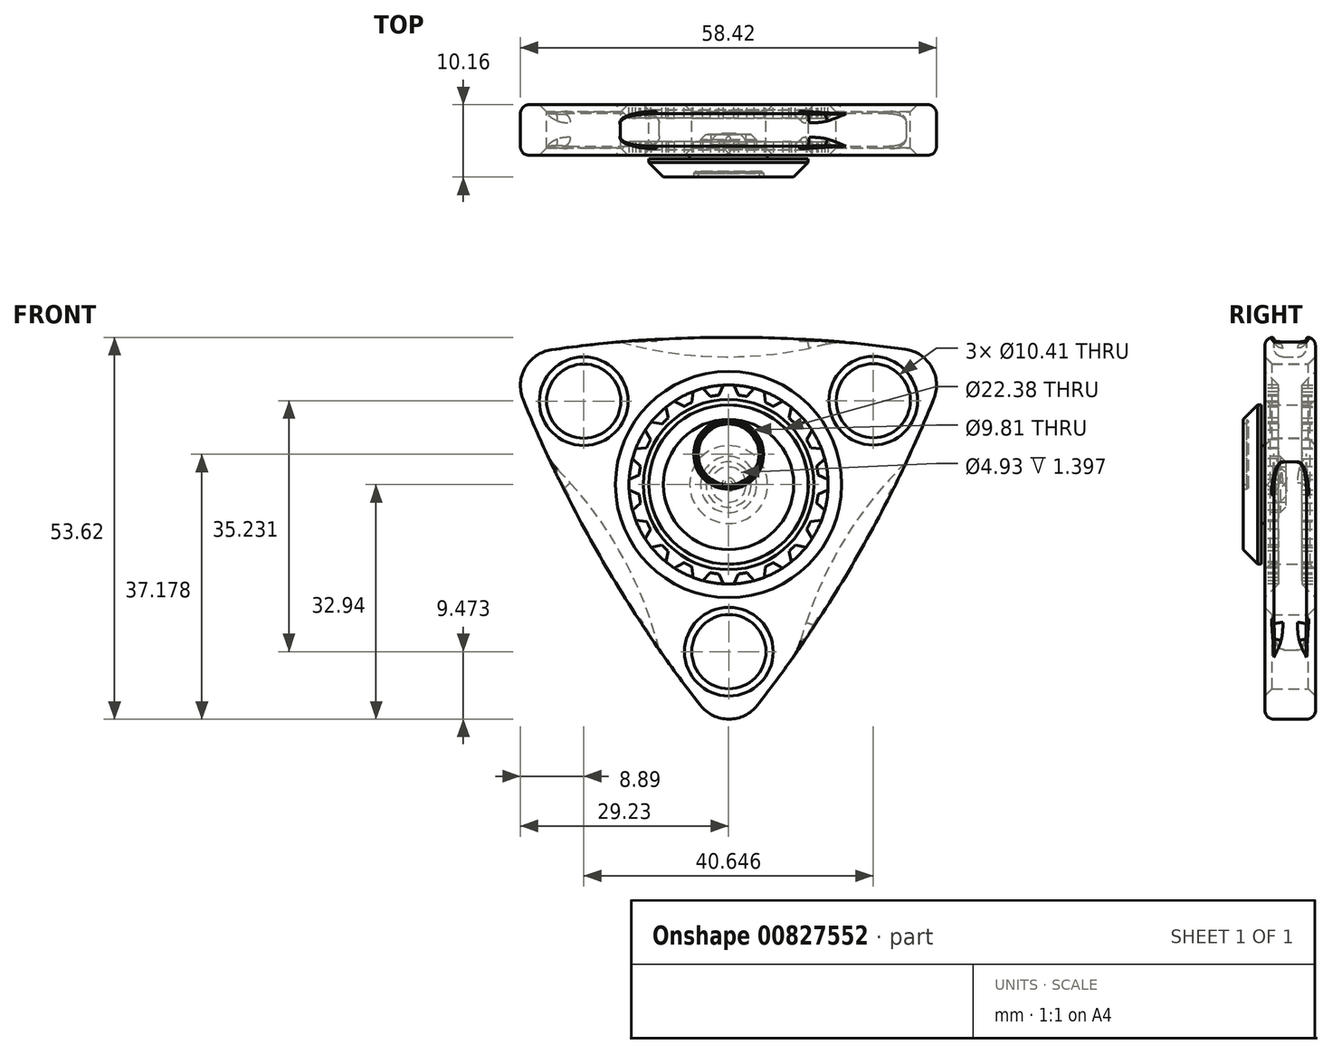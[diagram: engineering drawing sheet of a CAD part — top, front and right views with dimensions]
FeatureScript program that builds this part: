
annotation { "Feature Type Name" : "Feature", "Feature Type Description" : "" }
export const myFeature = defineFeature(function(context is Context, id is Id, definition is map)
    precondition{}
    {
        {
            var Q0;
            Q0=qCreatedBy(makeId("Front.planeOp"),FACE);
            var sketch = newSketch(context, id + "F0", { "sketchPlane" : qUnion([Q0])});
            skCircle(sketch, "E0", {"center": v(0, 0) * mm, "radius": 11.19 * mm});
            skCircle(sketch, "E1", {"center": v(0, 0) * mm, "radius": 14.4 * mm});
            skCircle(sketch, "E2.cCircle", {"center": v(0, 0) * mm, "radius": 17.96 * mm, "construction": true});
            skLineSegment(sketch, "E2.0", {"start": v(-31.13, 17.91) * mm, "end": v(31.08, 18) * mm});
            skLineSegment(sketch, "E2.1", {"start": v(31.08, 18) * mm, "end": v(0.05, -35.92) * mm});
            skLineSegment(sketch, "E2.2", {"start": v(0.05, -35.92) * mm, "end": v(-31.13, 17.91) * mm});
            skPoint(sketch, "E2.0.midPoint", {"position": v(-0.03, 17.96) * mm});
            skArc(sketch, "E3", {"start": v(31.08, 18) * mm, "mid": v(-0.03, 20.7) * mm, "end": v(-31.13, 17.91) * mm});
            skArc(sketch, "E4.1.0", {"start": v(-31.13, 17.91) * mm, "mid": v(-17.92, -10.38) * mm, "end": v(0.05, -35.92) * mm});
            skArc(sketch, "E4.2.0", {"start": v(0.05, -35.92) * mm, "mid": v(17.95, -10.33) * mm, "end": v(31.08, 18) * mm});
            skLineSegment(sketch, "E5", {"start": v(0, 0) * mm, "end": v(-31.13, 17.91) * mm});
            skCircle(sketch, "E6", {"center": v(-20.34, 11.7) * mm, "radius": 5.2 * mm});
            skCircle(sketch, "E7.1.0", {"center": v(0.03, -23.47) * mm, "radius": 5.2 * mm});
            skCircle(sketch, "E7.2.0", {"center": v(20.3, 11.76) * mm, "radius": 5.2 * mm});
            skSolve(sketch);
        }
        {
            var Q0;
            Q0=makeQuery(id+"F0.imprint","IMPRINT",FACE,{"disambiguationData":[TD([[makeQuery(id+"F0.imprint","IMPRINT",EDGE,{"derivedFrom":sQuery(id+"F0.wireOp",EDGE,"E1")}),-1.0]])]});
            var Q1;
            Q1=makeQuery(id+"F0.imprint","IMPRINT",FACE,{"disambiguationData":[TD([[makeQuery(id+"F0.imprint","IMPRINT",EDGE,{"derivedFrom":sQuery(id+"F0.wireOp",EDGE,"E0")}),-1.0]])]});
            var Q2;
            Q2=makeQuery(id+"F0.imprint","IMPRINT",FACE,{"disambiguationData":[TD([[makeQuery(id+"F0.imprint","IMPRINT",EDGE,{"derivedFrom":sQuery(id+"F0.wireOp",EDGE,"E2.2")}),1.0]])]});
            var Q3;
            Q3=makeQuery(id+"F0.imprint","IMPRINT",FACE,{"disambiguationData":[TD([[makeQuery(id+"F0.imprint","IMPRINT",EDGE,{"derivedFrom":sQuery(id+"F0.wireOp",EDGE,"E2.0")}),1.0]])]});
            var Q4;
            Q4=makeQuery(id+"F0.imprint","IMPRINT",FACE,{"disambiguationData":[TD([[makeQuery(id+"F0.imprint","IMPRINT",EDGE,{"derivedFrom":sQuery(id+"F0.wireOp",EDGE,"E2.1")}),1.0]])]});
            extrude(context, id + "F1", {"entities" : qUnion([Q0, Q1, Q2, Q3, Q4]), "depth" : 3.56 * mm, "offsetDistance" : 25.4 * mm});
        }
        {
            var Q0;
            Q0=makeQuery(id+"F1.opExtrude","SWEPT_EDGE",EDGE,{"disambiguationData":[OSD([sQuery(id+"F0.wireOp",EDGE,"E2.0"),sQuery(id+"F0.wireOp",EDGE,"E2.2"),sQuery(id+"F0.wireOp",EDGE,"E3"),sQuery(id+"F0.wireOp",EDGE,"E4.1.0")])]});
            var Q1;
            Q1=makeQuery(id+"F1.opExtrude","SWEPT_EDGE",EDGE,{"disambiguationData":[OSD([sQuery(id+"F0.wireOp",EDGE,"E2.1"),sQuery(id+"F0.wireOp",EDGE,"E2.2"),sQuery(id+"F0.wireOp",EDGE,"E4.1.0"),sQuery(id+"F0.wireOp",EDGE,"E4.2.0")])]});
            var Q2;
            Q2=makeQuery(id+"F1.opExtrude","SWEPT_EDGE",EDGE,{"disambiguationData":[OSD([sQuery(id+"F0.wireOp",EDGE,"E2.0"),sQuery(id+"F0.wireOp",EDGE,"E2.1"),sQuery(id+"F0.wireOp",EDGE,"E3"),sQuery(id+"F0.wireOp",EDGE,"E4.2.0")])]});
            fillet(context, id + "F2", {"entities" : qUnion([Q0, Q1, Q2]), "radius" : 5.08 * mm, "tangentPropagation" : true, "allowEdgeOverflow" : false});
        }
        {
            var Q0;
            Q0=makeQuery(id+"F1.opExtrude","CAP_EDGE",EDGE,{"disambiguationData":[OSD([sQuery(id+"F0.wireOp",EDGE,"E6")])],"isStart":false});
            var Q1;
            Q1=makeQuery(id+"F1.opExtrude","CAP_EDGE",EDGE,{"disambiguationData":[OSD([sQuery(id+"F0.wireOp",EDGE,"E7.2.0")])],"isStart":false});
            var Q2;
            Q2=makeQuery(id+"F1.opExtrude","CAP_EDGE",EDGE,{"disambiguationData":[OSD([sQuery(id+"F0.wireOp",EDGE,"E7.1.0")])],"isStart":false});
            chamfer(context, id + "F3", {"entities" : qUnion([Q0, Q1, Q2]), "width" : 1.02 * mm, "tangentPropagation" : true});
        }
        {
            var Q0;
            Q0=makeQuery(id+"F1.opExtrude","CAP_EDGE",EDGE,{"disambiguationData":[OSD([sQuery(id+"F0.wireOp",EDGE,"E4.2.0")])],"isStart":false});
            var Q1;
            Q1=makeQuery(id+"F1.opExtrude","CAP_EDGE",EDGE,{"disambiguationData":[OSD([sQuery(id+"F0.wireOp",EDGE,"E4.1.0")])],"isStart":false});
            var Q2;
            Q2=makeQuery(id+"F1.opExtrude","CAP_EDGE",EDGE,{"disambiguationData":[OSD([sQuery(id+"F0.wireOp",EDGE,"E3")])],"isStart":false});
            fillet(context, id + "F4", {"entities" : qUnion([Q0, Q1, Q2]), "radius" : 1.27 * mm, "tangentPropagation" : true, "allowEdgeOverflow" : false});
        }
        {
            var Q0;
            Q0=makeQuery(id+"F1.opExtrude","CAP_FACE",FACE,{"disambiguationData":[OSD([sQuery(id+"F0.wireOp",EDGE,"E0"),sQuery(id+"F0.wireOp",EDGE,"E3"),sQuery(id+"F0.wireOp",EDGE,"E4.1.0"),sQuery(id+"F0.wireOp",EDGE,"E4.2.0"),sQuery(id+"F0.wireOp",EDGE,"E6"),sQuery(id+"F0.wireOp",EDGE,"E7.1.0"),sQuery(id+"F0.wireOp",EDGE,"E7.2.0")])],"isStart":false});
            var sketch = newSketch(context, id + "F5", { "sketchPlane" : qUnion([Q0])});
            skCircle(sketch, "E8", {"center": v(0, 0) * mm, "radius": 12.63 * mm});
            skCircle(sketch, "E9", {"center": v(0, 0) * mm, "radius": 15.88 * mm});
            skLineSegment(sketch, "E10", {"start": v(-1.37, 12.56) * mm, "end": v(-0.73, 13.97) * mm});
            skLineSegment(sketch, "E11.MirrorCS", {"start": v(1.37, 12.56) * mm, "end": v(0.73, 13.97) * mm});
            skLineSegment(sketch, "E12", {"start": v(-0.73, 13.97) * mm, "end": v(0.73, 13.97) * mm});
            skLineSegment(sketch, "E13.1.0", {"start": v(-5.19, 11.52) * mm, "end": v(-5, 13.06) * mm});
            skLineSegment(sketch, "E13.1.1", {"start": v(-2.57, 12.37) * mm, "end": v(-3.62, 13.5) * mm});
            skLineSegment(sketch, "E13.1.2", {"start": v(-5, 13.06) * mm, "end": v(-3.62, 13.5) * mm});
            skLineSegment(sketch, "E13.2.0", {"start": v(-8.5, 9.35) * mm, "end": v(-8.8, 10.87) * mm});
            skLineSegment(sketch, "E13.2.1", {"start": v(-6.27, 10.96) * mm, "end": v(-7.62, 11.73) * mm});
            skLineSegment(sketch, "E13.2.2", {"start": v(-8.8, 10.87) * mm, "end": v(-7.62, 11.73) * mm});
            skLineSegment(sketch, "E13.3.0", {"start": v(-10.96, 6.27) * mm, "end": v(-11.73, 7.62) * mm});
            skLineSegment(sketch, "E13.3.1", {"start": v(-9.35, 8.5) * mm, "end": v(-10.87, 8.8) * mm});
            skLineSegment(sketch, "E13.3.2", {"start": v(-11.73, 7.62) * mm, "end": v(-10.87, 8.8) * mm});
            skLineSegment(sketch, "E13.4.0", {"start": v(-12.37, 2.57) * mm, "end": v(-13.5, 3.62) * mm});
            skLineSegment(sketch, "E13.4.1", {"start": v(-11.52, 5.19) * mm, "end": v(-13.06, 5) * mm});
            skLineSegment(sketch, "E13.4.2", {"start": v(-13.5, 3.62) * mm, "end": v(-13.06, 5) * mm});
            skLineSegment(sketch, "E13.5.0", {"start": v(-12.56, -1.37) * mm, "end": v(-13.97, -0.73) * mm});
            skLineSegment(sketch, "E13.5.1", {"start": v(-12.56, 1.37) * mm, "end": v(-13.97, 0.73) * mm});
            skLineSegment(sketch, "E13.5.2", {"start": v(-13.97, -0.73) * mm, "end": v(-13.97, 0.73) * mm});
            skLineSegment(sketch, "E13.6.0", {"start": v(-11.52, -5.19) * mm, "end": v(-13.06, -5) * mm});
            skLineSegment(sketch, "E13.6.1", {"start": v(-12.37, -2.57) * mm, "end": v(-13.5, -3.62) * mm});
            skLineSegment(sketch, "E13.6.2", {"start": v(-13.06, -5) * mm, "end": v(-13.5, -3.62) * mm});
            skLineSegment(sketch, "E13.7.0", {"start": v(-9.35, -8.5) * mm, "end": v(-10.87, -8.8) * mm});
            skLineSegment(sketch, "E13.7.1", {"start": v(-10.96, -6.27) * mm, "end": v(-11.73, -7.62) * mm});
            skLineSegment(sketch, "E13.7.2", {"start": v(-10.87, -8.8) * mm, "end": v(-11.73, -7.62) * mm});
            skLineSegment(sketch, "E13.8.0", {"start": v(-6.27, -10.96) * mm, "end": v(-7.62, -11.73) * mm});
            skLineSegment(sketch, "E13.8.1", {"start": v(-8.5, -9.35) * mm, "end": v(-8.8, -10.87) * mm});
            skLineSegment(sketch, "E13.8.2", {"start": v(-7.62, -11.73) * mm, "end": v(-8.8, -10.87) * mm});
            skLineSegment(sketch, "E13.9.0", {"start": v(-2.57, -12.37) * mm, "end": v(-3.62, -13.5) * mm});
            skLineSegment(sketch, "E13.9.1", {"start": v(-5.19, -11.52) * mm, "end": v(-5, -13.06) * mm});
            skLineSegment(sketch, "E13.9.2", {"start": v(-3.62, -13.5) * mm, "end": v(-5, -13.06) * mm});
            skLineSegment(sketch, "E13.10.0", {"start": v(1.37, -12.56) * mm, "end": v(0.73, -13.97) * mm});
            skLineSegment(sketch, "E13.10.1", {"start": v(-1.37, -12.56) * mm, "end": v(-0.73, -13.97) * mm});
            skLineSegment(sketch, "E13.10.2", {"start": v(0.73, -13.97) * mm, "end": v(-0.73, -13.97) * mm});
            skLineSegment(sketch, "E13.11.0", {"start": v(5.19, -11.52) * mm, "end": v(5, -13.06) * mm});
            skLineSegment(sketch, "E13.11.1", {"start": v(2.57, -12.37) * mm, "end": v(3.62, -13.5) * mm});
            skLineSegment(sketch, "E13.11.2", {"start": v(5, -13.06) * mm, "end": v(3.62, -13.5) * mm});
            skLineSegment(sketch, "E13.12.0", {"start": v(8.5, -9.35) * mm, "end": v(8.8, -10.87) * mm});
            skLineSegment(sketch, "E13.12.1", {"start": v(6.27, -10.96) * mm, "end": v(7.62, -11.73) * mm});
            skLineSegment(sketch, "E13.12.2", {"start": v(8.8, -10.87) * mm, "end": v(7.62, -11.73) * mm});
            skLineSegment(sketch, "E13.13.0", {"start": v(10.96, -6.27) * mm, "end": v(11.73, -7.62) * mm});
            skLineSegment(sketch, "E13.13.1", {"start": v(9.35, -8.5) * mm, "end": v(10.87, -8.8) * mm});
            skLineSegment(sketch, "E13.13.2", {"start": v(11.73, -7.62) * mm, "end": v(10.87, -8.8) * mm});
            skLineSegment(sketch, "E13.14.0", {"start": v(12.37, -2.57) * mm, "end": v(13.5, -3.62) * mm});
            skLineSegment(sketch, "E13.14.1", {"start": v(11.52, -5.19) * mm, "end": v(13.06, -5) * mm});
            skLineSegment(sketch, "E13.14.2", {"start": v(13.5, -3.62) * mm, "end": v(13.06, -5) * mm});
            skLineSegment(sketch, "E13.15.0", {"start": v(12.56, 1.37) * mm, "end": v(13.97, 0.73) * mm});
            skLineSegment(sketch, "E13.15.1", {"start": v(12.56, -1.37) * mm, "end": v(13.97, -0.73) * mm});
            skLineSegment(sketch, "E13.15.2", {"start": v(13.97, 0.73) * mm, "end": v(13.97, -0.73) * mm});
            skLineSegment(sketch, "E13.16.0", {"start": v(11.52, 5.19) * mm, "end": v(13.06, 5) * mm});
            skLineSegment(sketch, "E13.16.1", {"start": v(12.37, 2.57) * mm, "end": v(13.5, 3.62) * mm});
            skLineSegment(sketch, "E13.16.2", {"start": v(13.06, 5) * mm, "end": v(13.5, 3.62) * mm});
            skLineSegment(sketch, "E13.17.0", {"start": v(9.35, 8.5) * mm, "end": v(10.87, 8.8) * mm});
            skLineSegment(sketch, "E13.17.1", {"start": v(10.96, 6.27) * mm, "end": v(11.73, 7.62) * mm});
            skLineSegment(sketch, "E13.17.2", {"start": v(10.87, 8.8) * mm, "end": v(11.73, 7.62) * mm});
            skLineSegment(sketch, "E13.18.0", {"start": v(6.27, 10.96) * mm, "end": v(7.62, 11.73) * mm});
            skLineSegment(sketch, "E13.18.1", {"start": v(8.5, 9.35) * mm, "end": v(8.8, 10.87) * mm});
            skLineSegment(sketch, "E13.18.2", {"start": v(7.62, 11.73) * mm, "end": v(8.8, 10.87) * mm});
            skLineSegment(sketch, "E13.19.0", {"start": v(2.57, 12.37) * mm, "end": v(3.62, 13.5) * mm});
            skLineSegment(sketch, "E13.19.1", {"start": v(5.19, 11.52) * mm, "end": v(5, 13.06) * mm});
            skLineSegment(sketch, "E13.19.2", {"start": v(3.62, 13.5) * mm, "end": v(5, 13.06) * mm});
            skSolve(sketch);
        }
        {
            var Q0;
            Q0=makeQuery(id+"F5.imprint","IMPRINT",FACE,{"disambiguationData":[TD([[makeQuery(id+"F5.imprint","IMPRINT",EDGE,{"derivedFrom":sQuery(id+"F5.wireOp",EDGE,"E8")}),-1.0]])]});
            extrude(context, id + "F6", {"entities" : qUnion([Q0]), "operationType" : NewBodyOperationType.REMOVE, "oppositeDirection" : true, "depth" : 1.9 * mm, "offsetDistance" : 25.4 * mm});
        }
        {
            var Q0;
            Q0=makeQuery(id+"F6.boolean.opBoolean","COPY",EDGE,{"derivedFrom":makeQuery(id+"F6.opExtrude","CAP_EDGE",EDGE,{"disambiguationData":[OSD([sQuery(id+"F5.wireOp",EDGE,"E9")])],"isStart":false})});
            chamfer(context, id + "F7", {"entities" : qUnion([Q0]), "width" : 1.9 * mm, "tangentPropagation" : true});
        }
        {
            var Q0;
            Q0=makeQuery(id+"F1.opExtrude","CAP_EDGE",EDGE,{"disambiguationData":[OSD([sQuery(id+"F0.wireOp",EDGE,"E0")])],"isStart":false});
            chamfer(context, id + "F8", {"entities" : qUnion([Q0]), "width" : 0.76 * mm, "tangentPropagation" : true});
        }
        {
            var Q0;
            Q0=makeQuery(id+"F1.opExtrude","CAP_FACE",FACE,{"disambiguationData":[OSD([sQuery(id+"F0.wireOp",EDGE,"E0"),sQuery(id+"F0.wireOp",EDGE,"E3"),sQuery(id+"F0.wireOp",EDGE,"E4.1.0"),sQuery(id+"F0.wireOp",EDGE,"E4.2.0"),sQuery(id+"F0.wireOp",EDGE,"E6"),sQuery(id+"F0.wireOp",EDGE,"E7.1.0"),sQuery(id+"F0.wireOp",EDGE,"E7.2.0")])],"isStart":true});
            var sketch = newSketch(context, id + "F9", { "sketchPlane" : qUnion([Q0])});
            skLineSegment(sketch, "E14", {"start": v(-20.3, 11.76) * mm, "end": v(20.34, 11.7) * mm});
            skLineSegment(sketch, "E15", {"start": v(-15.1, 11.76) * mm, "end": v(-15.1, 24.64) * mm});
            skLineSegment(sketch, "E16", {"start": v(15.13, 11.76) * mm, "end": v(15.27, 23.47) * mm});
            skArc(sketch, "E17", {"start": v(-15.1, 20.08) * mm, "mid": v(0.06, 17.93) * mm, "end": v(15.23, 20.03) * mm});
            skLineSegment(sketch, "E18", {"start": v(-15.1, 24.64) * mm, "end": v(15.27, 23.47) * mm});
            skLineSegment(sketch, "E19.1.0", {"start": v(-13.8, -25.4) * mm, "end": v(-27.96, 1.49) * mm});
            skLineSegment(sketch, "E19.1.1", {"start": v(-2.64, -18.96) * mm, "end": v(-13.8, -25.4) * mm});
            skArc(sketch, "E19.1.2", {"start": v(-9.84, -23.12) * mm, "mid": v(-15.56, -8.91) * mm, "end": v(-24.96, 3.17) * mm});
            skLineSegment(sketch, "E19.1.3", {"start": v(-17.75, 7.22) * mm, "end": v(-27.96, 1.49) * mm});
            skLineSegment(sketch, "E19.2.0", {"start": v(28.9, 0.75) * mm, "end": v(12.7, -24.96) * mm});
            skLineSegment(sketch, "E19.2.1", {"start": v(17.74, 7.2) * mm, "end": v(28.9, 0.75) * mm});
            skArc(sketch, "E19.2.2", {"start": v(24.94, 3.03) * mm, "mid": v(15.5, -9.02) * mm, "end": v(9.73, -23.2) * mm});
            skLineSegment(sketch, "E19.2.3", {"start": v(2.62, -18.99) * mm, "end": v(12.7, -24.96) * mm});
            skPoint(sketch, "E19.center", {"position": v(0, 0) * mm});
            skSolve(sketch);
        }
        {
            var Q0;
            {var subQ0=sQuery(id+"F9.wireOp",EDGE,"E17");Q0=makeQuery(id+"F9.imprint","IMPRINT",FACE,{"disambiguationData":[TD([[makeQuery(id+"F9.imprint","IMPRINT",EDGE,{"derivedFrom":subQ0}),1.0]])]});}
            var Q1;
            {var subQ0=sQuery(id+"F9.wireOp",EDGE,"E19.1.2");Q1=makeQuery(id+"F9.imprint","IMPRINT",FACE,{"disambiguationData":[TD([[makeQuery(id+"F9.imprint","IMPRINT",EDGE,{"derivedFrom":subQ0}),1.0]])]});}
            var Q2;
            {var subQ0=sQuery(id+"F9.wireOp",EDGE,"E19.1.0");Q2=makeQuery(id+"F9.imprint","IMPRINT",FACE,{"disambiguationData":[TD([[makeQuery(id+"F9.imprint","IMPRINT",EDGE,{"derivedFrom":subQ0}),-1.0]])]});}
            var Q3;
            {var subQ0=sQuery(id+"F9.wireOp",EDGE,"E18");Q3=makeQuery(id+"F9.imprint","IMPRINT",FACE,{"disambiguationData":[TD([[makeQuery(id+"F9.imprint","IMPRINT",EDGE,{"derivedFrom":subQ0}),-1.0]])]});}
            var Q4;
            {var subQ0=sQuery(id+"F9.wireOp",EDGE,"E19.2.0");Q4=makeQuery(id+"F9.imprint","IMPRINT",FACE,{"disambiguationData":[TD([[makeQuery(id+"F9.imprint","IMPRINT",EDGE,{"derivedFrom":subQ0}),-1.0]])]});}
            var Q5;
            {var subQ0=sQuery(id+"F9.wireOp",EDGE,"E19.2.2");Q5=makeQuery(id+"F9.imprint","IMPRINT",FACE,{"disambiguationData":[TD([[makeQuery(id+"F9.imprint","IMPRINT",EDGE,{"derivedFrom":subQ0}),1.0]])]});}
            extrude(context, id + "F10", {"entities" : qUnion([Q0, Q1, Q2, Q3, Q4, Q5]), "operationType" : NewBodyOperationType.REMOVE, "oppositeDirection" : true, "depth" : 2.3 * mm, "offsetDistance" : 25.4 * mm});
        }
        {
            var Q0;
            Q0=makeQuery(id+"F1.opExtrude","SWEPT_BODY",BODY,{"disambiguationData":[OSD([sQuery(id+"F0.wireOp",EDGE,"E0"),sQuery(id+"F0.wireOp",EDGE,"E3"),sQuery(id+"F0.wireOp",EDGE,"E4.1.0"),sQuery(id+"F0.wireOp",EDGE,"E4.2.0"),sQuery(id+"F0.wireOp",EDGE,"E6"),sQuery(id+"F0.wireOp",EDGE,"E7.1.0"),sQuery(id+"F0.wireOp",EDGE,"E7.2.0")])]});
            var Q1;
            Q1=qCreatedBy(makeId("Front.planeOp"),FACE);
            mirror(context, id + "F11", {"operationType" : NewBodyOperationType.ADD, "entities" : qUnion([Q0]), "mirrorPlane" : qUnion([Q1])});
        }
        {
            var Q0;
            {var subQ0=makeQuery(id+"F10.boolean.opBoolean","COPY",EDGE,{"derivedFrom":makeQuery(id+"F10.opExtrude","SWEPT_EDGE",EDGE,{"disambiguationData":[OSD([sQuery(id+"F0.wireOp",EDGE,"E3"),sQuery(id+"F9.wireOp",EDGE,"E16"),sQuery(id+"F9.wireOp",EDGE,"E17")])]})});Q0=makeQuery(id+"F11.boolean.opBoolean","MERGE",EDGE,{"derivedFrom":[subQ0,makeQuery(id+"F11.opPattern","COPY",EDGE,{"derivedFrom":subQ0,"instanceName":"1"})]});}
            var Q1;
            {var subQ0=makeQuery(id+"F10.boolean.opBoolean","COPY",EDGE,{"derivedFrom":makeQuery(id+"F10.opExtrude","SWEPT_EDGE",EDGE,{"disambiguationData":[OSD([sQuery(id+"F0.wireOp",EDGE,"E3"),sQuery(id+"F9.wireOp",EDGE,"E15"),sQuery(id+"F9.wireOp",EDGE,"E17")])]})});Q1=makeQuery(id+"F11.boolean.opBoolean","MERGE",EDGE,{"derivedFrom":[subQ0,makeQuery(id+"F11.opPattern","COPY",EDGE,{"derivedFrom":subQ0,"instanceName":"1"})]});}
            var Q2;
            {var subQ0=makeQuery(id+"F10.boolean.opBoolean","COPY",EDGE,{"derivedFrom":makeQuery(id+"F10.opExtrude","SWEPT_EDGE",EDGE,{"disambiguationData":[OSD([sQuery(id+"F0.wireOp",EDGE,"E4.1.0"),sQuery(id+"F9.wireOp",EDGE,"E19.2.1"),sQuery(id+"F9.wireOp",EDGE,"E19.2.2")])]})});Q2=makeQuery(id+"F11.boolean.opBoolean","MERGE",EDGE,{"derivedFrom":[subQ0,makeQuery(id+"F11.opPattern","COPY",EDGE,{"derivedFrom":subQ0,"instanceName":"1"})]});}
            var Q3;
            {var subQ0=makeQuery(id+"F10.boolean.opBoolean","COPY",EDGE,{"derivedFrom":makeQuery(id+"F10.opExtrude","SWEPT_EDGE",EDGE,{"disambiguationData":[OSD([sQuery(id+"F0.wireOp",EDGE,"E4.1.0"),sQuery(id+"F9.wireOp",EDGE,"E19.2.2"),sQuery(id+"F9.wireOp",EDGE,"E19.2.3")])]})});Q3=makeQuery(id+"F11.boolean.opBoolean","MERGE",EDGE,{"derivedFrom":[subQ0,makeQuery(id+"F11.opPattern","COPY",EDGE,{"derivedFrom":subQ0,"instanceName":"1"})]});}
            var Q4;
            {var subQ0=makeQuery(id+"F10.boolean.opBoolean","COPY",EDGE,{"derivedFrom":makeQuery(id+"F10.opExtrude","SWEPT_EDGE",EDGE,{"disambiguationData":[OSD([sQuery(id+"F0.wireOp",EDGE,"E4.2.0"),sQuery(id+"F9.wireOp",EDGE,"E19.1.1"),sQuery(id+"F9.wireOp",EDGE,"E19.1.2")])]})});Q4=makeQuery(id+"F11.boolean.opBoolean","MERGE",EDGE,{"derivedFrom":[subQ0,makeQuery(id+"F11.opPattern","COPY",EDGE,{"derivedFrom":subQ0,"instanceName":"1"})]});}
            var Q5;
            {var subQ0=makeQuery(id+"F10.boolean.opBoolean","COPY",EDGE,{"derivedFrom":makeQuery(id+"F10.opExtrude","SWEPT_EDGE",EDGE,{"disambiguationData":[OSD([sQuery(id+"F0.wireOp",EDGE,"E4.2.0"),sQuery(id+"F9.wireOp",EDGE,"E19.1.2"),sQuery(id+"F9.wireOp",EDGE,"E19.1.3")])]})});Q5=makeQuery(id+"F11.boolean.opBoolean","MERGE",EDGE,{"derivedFrom":[subQ0,makeQuery(id+"F11.opPattern","COPY",EDGE,{"derivedFrom":subQ0,"instanceName":"1"})]});}
            fillet(context, id + "F12", {"entities" : qUnion([Q0, Q1, Q2, Q3, Q4, Q5]), "radius" : 7.62 * mm, "tangentPropagation" : true, "allowEdgeOverflow" : false});
        }
        {
            var Q0;
            Q0=makeQuery(id+"F11.opPattern","COPY",EDGE,{"derivedFrom":makeQuery(id+"F10.boolean.opBoolean","COPY",EDGE,{"derivedFrom":makeQuery(id+"F10.opExtrude","CAP_EDGE",EDGE,{"disambiguationData":[OSD([sQuery(id+"F9.wireOp",EDGE,"E19.1.2")])],"isStart":false})}),"instanceName":"1"});
            var Q1;
            Q1=makeQuery(id+"F10.boolean.opBoolean","COPY",EDGE,{"derivedFrom":makeQuery(id+"F10.opExtrude","CAP_EDGE",EDGE,{"disambiguationData":[OSD([sQuery(id+"F9.wireOp",EDGE,"E19.1.2")])],"isStart":false})});
            var Q2;
            Q2=makeQuery(id+"F11.opPattern","COPY",EDGE,{"derivedFrom":makeQuery(id+"F10.boolean.opBoolean","COPY",EDGE,{"derivedFrom":makeQuery(id+"F10.opExtrude","CAP_EDGE",EDGE,{"disambiguationData":[OSD([sQuery(id+"F9.wireOp",EDGE,"E19.2.2")])],"isStart":false})}),"instanceName":"1"});
            var Q3;
            Q3=makeQuery(id+"F10.boolean.opBoolean","COPY",EDGE,{"derivedFrom":makeQuery(id+"F10.opExtrude","CAP_EDGE",EDGE,{"disambiguationData":[OSD([sQuery(id+"F9.wireOp",EDGE,"E19.2.2")])],"isStart":false})});
            var Q4;
            Q4=makeQuery(id+"F11.opPattern","COPY",EDGE,{"derivedFrom":makeQuery(id+"F10.boolean.opBoolean","COPY",EDGE,{"derivedFrom":makeQuery(id+"F10.opExtrude","CAP_EDGE",EDGE,{"disambiguationData":[OSD([sQuery(id+"F9.wireOp",EDGE,"E17")])],"isStart":false})}),"instanceName":"1"});
            var Q5;
            Q5=makeQuery(id+"F10.boolean.opBoolean","COPY",EDGE,{"derivedFrom":makeQuery(id+"F10.opExtrude","CAP_EDGE",EDGE,{"disambiguationData":[OSD([sQuery(id+"F9.wireOp",EDGE,"E17")])],"isStart":false})});
            fillet(context, id + "F13", {"entities" : qUnion([Q0, Q1, Q2, Q3, Q4, Q5]), "radius" : 1.27 * mm, "tangentPropagation" : true, "allowEdgeOverflow" : false});
        }
        {
            var Q0;
            {var subQ0=sQuery(id+"F0.wireOp",EDGE,"E3");var subQ1=makeQuery(id+"F4.opFillet","BLEND_FACE",FACE,{"disambiguationData":[OSD([subQ0])]});var subQ5=sQuery(id+"F0.wireOp",EDGE,"E4.2.0");var subQ6=sQuery(id+"F0.wireOp",EDGE,"E4.1.0");var subQ7=sQuery(id+"F0.wireOp",EDGE,"E2.1");var subQ8=sQuery(id+"F0.wireOp",EDGE,"E2.0");var subQ10=makeQuery(id+"F1.opExtrude","SWEPT_FACE",FACE,{"disambiguationData":[OSD([subQ0])]});var subQ11=sQuery(id+"F9.wireOp",EDGE,"E17");var subQ12=makeQuery(id+"F10.opExtrude","CAP_FACE",FACE,{"disambiguationData":[OSD([sQuery(id+"F9.wireOp",EDGE,"E15"),sQuery(id+"F9.wireOp",EDGE,"E16"),subQ11,sQuery(id+"F9.wireOp",EDGE,"E18")])],"isStart":false});var subQ14=makeQuery(id+"F4.opFillet","BLEND_EDGE",EDGE,{"blendedFrom":[makeQuery(id+"F1.opExtrude","CAP_EDGE",EDGE,{"disambiguationData":[OSD([subQ0])],"isStart":false}),subQ10],"blendedInto":[subQ10]});var subQ15=sQuery(id+"F0.wireOp",EDGE,"E2.2");Q0=makeQuery(id+"F12.opFillet","MERGE",EDGE,{"derivedFrom":[makeQuery(id+"F10.boolean.opBoolean","SPLIT",EDGE,{"disambiguationData":[topologyDisambiguationEdgeConnected([subQ1,subQ12])],"derivedFrom":subQ14}),makeQuery(id+"F10.boolean.opBoolean","SPLIT",EDGE,{"disambiguationData":[topologyDisambiguationEdgeConnected([subQ10,subQ1]),TD([makeQuery(id+"F2.opFillet","BLEND_FACE",FACE,{"disambiguationData":[OSD([subQ8,subQ15,subQ0,subQ6])]})])],"derivedFrom":subQ14}),makeQuery(id+"F10.boolean.opBoolean","SPLIT",EDGE,{"disambiguationData":[topologyDisambiguationEdgeConnected([subQ10,subQ1]),TD([makeQuery(id+"F2.opFillet","BLEND_FACE",FACE,{"disambiguationData":[OSD([subQ8,subQ7,subQ0,subQ5])]})])],"derivedFrom":subQ14})]});}
            var Q1;
            {var subQ0=sQuery(id+"F0.wireOp",EDGE,"E3");var subQ1=makeQuery(id+"F4.opFillet","BLEND_FACE",FACE,{"disambiguationData":[OSD([subQ0])]});var subQ5=sQuery(id+"F0.wireOp",EDGE,"E4.2.0");var subQ6=sQuery(id+"F0.wireOp",EDGE,"E4.1.0");var subQ7=sQuery(id+"F0.wireOp",EDGE,"E2.1");var subQ8=sQuery(id+"F0.wireOp",EDGE,"E2.0");var subQ10=makeQuery(id+"F1.opExtrude","SWEPT_FACE",FACE,{"disambiguationData":[OSD([subQ0])]});var subQ11=sQuery(id+"F9.wireOp",EDGE,"E17");var subQ12=makeQuery(id+"F10.opExtrude","CAP_FACE",FACE,{"disambiguationData":[OSD([sQuery(id+"F9.wireOp",EDGE,"E15"),sQuery(id+"F9.wireOp",EDGE,"E16"),subQ11,sQuery(id+"F9.wireOp",EDGE,"E18")])],"isStart":false});var subQ14=makeQuery(id+"F4.opFillet","BLEND_EDGE",EDGE,{"blendedFrom":[makeQuery(id+"F1.opExtrude","CAP_EDGE",EDGE,{"disambiguationData":[OSD([subQ0])],"isStart":false}),subQ10],"blendedInto":[subQ10]});var subQ15=sQuery(id+"F0.wireOp",EDGE,"E2.2");Q1=makeQuery(id+"F12.opFillet","MERGE",EDGE,{"derivedFrom":[makeQuery(id+"F11.opPattern","COPY",EDGE,{"derivedFrom":makeQuery(id+"F10.boolean.opBoolean","SPLIT",EDGE,{"disambiguationData":[topologyDisambiguationEdgeConnected([subQ1,subQ12])],"derivedFrom":subQ14}),"instanceName":"1"}),makeQuery(id+"F11.opPattern","COPY",EDGE,{"derivedFrom":makeQuery(id+"F10.boolean.opBoolean","SPLIT",EDGE,{"disambiguationData":[topologyDisambiguationEdgeConnected([subQ10,subQ1]),TD([makeQuery(id+"F2.opFillet","BLEND_FACE",FACE,{"disambiguationData":[OSD([subQ8,subQ15,subQ0,subQ6])]})])],"derivedFrom":subQ14}),"instanceName":"1"}),makeQuery(id+"F11.opPattern","COPY",EDGE,{"derivedFrom":makeQuery(id+"F10.boolean.opBoolean","SPLIT",EDGE,{"disambiguationData":[topologyDisambiguationEdgeConnected([subQ10,subQ1]),TD([makeQuery(id+"F2.opFillet","BLEND_FACE",FACE,{"disambiguationData":[OSD([subQ8,subQ7,subQ0,subQ5])]})])],"derivedFrom":subQ14}),"instanceName":"1"})]});}
            var Q2;
            {var subQ0=sQuery(id+"F0.wireOp",EDGE,"E4.2.0");var subQ1=makeQuery(id+"F4.opFillet","BLEND_FACE",FACE,{"disambiguationData":[OSD([subQ0])]});var subQ2=sQuery(id+"F0.wireOp",EDGE,"E4.1.0");var subQ3=sQuery(id+"F0.wireOp",EDGE,"E2.2");var subQ4=sQuery(id+"F0.wireOp",EDGE,"E2.1");var subQ8=sQuery(id+"F0.wireOp",EDGE,"E3");var subQ10=sQuery(id+"F9.wireOp",EDGE,"E19.1.2");var subQ12=makeQuery(id+"F1.opExtrude","SWEPT_FACE",FACE,{"disambiguationData":[OSD([subQ0])]});var subQ13=makeQuery(id+"F10.opExtrude","CAP_FACE",FACE,{"disambiguationData":[OSD([sQuery(id+"F9.wireOp",EDGE,"E19.1.0"),sQuery(id+"F9.wireOp",EDGE,"E19.1.1"),subQ10,sQuery(id+"F9.wireOp",EDGE,"E19.1.3")])],"isStart":false});var subQ14=makeQuery(id+"F4.opFillet","BLEND_EDGE",EDGE,{"blendedFrom":[makeQuery(id+"F1.opExtrude","CAP_EDGE",EDGE,{"disambiguationData":[OSD([subQ0])],"isStart":false}),subQ12],"blendedInto":[subQ12]});var subQ15=sQuery(id+"F0.wireOp",EDGE,"E2.0");Q2=makeQuery(id+"F12.opFillet","MERGE",EDGE,{"derivedFrom":[makeQuery(id+"F11.opPattern","COPY",EDGE,{"derivedFrom":makeQuery(id+"F10.boolean.opBoolean","SPLIT",EDGE,{"disambiguationData":[topologyDisambiguationEdgeConnected([subQ1,subQ13])],"derivedFrom":subQ14}),"instanceName":"1"}),makeQuery(id+"F11.opPattern","COPY",EDGE,{"derivedFrom":makeQuery(id+"F10.boolean.opBoolean","SPLIT",EDGE,{"disambiguationData":[topologyDisambiguationEdgeConnected([subQ12,subQ1]),TD([makeQuery(id+"F2.opFillet","BLEND_FACE",FACE,{"disambiguationData":[OSD([subQ15,subQ4,subQ8,subQ0])]})])],"derivedFrom":subQ14}),"instanceName":"1"}),makeQuery(id+"F11.opPattern","COPY",EDGE,{"derivedFrom":makeQuery(id+"F10.boolean.opBoolean","SPLIT",EDGE,{"disambiguationData":[topologyDisambiguationEdgeConnected([subQ12,subQ1]),TD([makeQuery(id+"F2.opFillet","BLEND_FACE",FACE,{"disambiguationData":[OSD([subQ4,subQ3,subQ2,subQ0])]})])],"derivedFrom":subQ14}),"instanceName":"1"})]});}
            var Q3;
            {var subQ0=sQuery(id+"F0.wireOp",EDGE,"E4.2.0");var subQ1=makeQuery(id+"F4.opFillet","BLEND_FACE",FACE,{"disambiguationData":[OSD([subQ0])]});var subQ2=sQuery(id+"F0.wireOp",EDGE,"E4.1.0");var subQ3=sQuery(id+"F0.wireOp",EDGE,"E2.2");var subQ4=sQuery(id+"F0.wireOp",EDGE,"E2.1");var subQ8=sQuery(id+"F0.wireOp",EDGE,"E3");var subQ10=sQuery(id+"F9.wireOp",EDGE,"E19.1.2");var subQ12=makeQuery(id+"F1.opExtrude","SWEPT_FACE",FACE,{"disambiguationData":[OSD([subQ0])]});var subQ13=makeQuery(id+"F10.opExtrude","CAP_FACE",FACE,{"disambiguationData":[OSD([sQuery(id+"F9.wireOp",EDGE,"E19.1.0"),sQuery(id+"F9.wireOp",EDGE,"E19.1.1"),subQ10,sQuery(id+"F9.wireOp",EDGE,"E19.1.3")])],"isStart":false});var subQ14=makeQuery(id+"F4.opFillet","BLEND_EDGE",EDGE,{"blendedFrom":[makeQuery(id+"F1.opExtrude","CAP_EDGE",EDGE,{"disambiguationData":[OSD([subQ0])],"isStart":false}),subQ12],"blendedInto":[subQ12]});var subQ15=sQuery(id+"F0.wireOp",EDGE,"E2.0");Q3=makeQuery(id+"F12.opFillet","MERGE",EDGE,{"derivedFrom":[makeQuery(id+"F10.boolean.opBoolean","SPLIT",EDGE,{"disambiguationData":[topologyDisambiguationEdgeConnected([subQ1,subQ13])],"derivedFrom":subQ14}),makeQuery(id+"F10.boolean.opBoolean","SPLIT",EDGE,{"disambiguationData":[topologyDisambiguationEdgeConnected([subQ12,subQ1]),TD([makeQuery(id+"F2.opFillet","BLEND_FACE",FACE,{"disambiguationData":[OSD([subQ15,subQ4,subQ8,subQ0])]})])],"derivedFrom":subQ14}),makeQuery(id+"F10.boolean.opBoolean","SPLIT",EDGE,{"disambiguationData":[topologyDisambiguationEdgeConnected([subQ12,subQ1]),TD([makeQuery(id+"F2.opFillet","BLEND_FACE",FACE,{"disambiguationData":[OSD([subQ4,subQ3,subQ2,subQ0])]})])],"derivedFrom":subQ14})]});}
            var Q4;
            {var subQ0=sQuery(id+"F0.wireOp",EDGE,"E4.1.0");var subQ1=makeQuery(id+"F4.opFillet","BLEND_FACE",FACE,{"disambiguationData":[OSD([subQ0])]});var subQ5=sQuery(id+"F0.wireOp",EDGE,"E4.2.0");var subQ6=sQuery(id+"F0.wireOp",EDGE,"E3");var subQ7=sQuery(id+"F0.wireOp",EDGE,"E2.2");var subQ8=sQuery(id+"F0.wireOp",EDGE,"E2.1");var subQ10=makeQuery(id+"F1.opExtrude","SWEPT_FACE",FACE,{"disambiguationData":[OSD([subQ0])]});var subQ11=sQuery(id+"F9.wireOp",EDGE,"E19.2.2");var subQ12=makeQuery(id+"F10.opExtrude","CAP_FACE",FACE,{"disambiguationData":[OSD([sQuery(id+"F9.wireOp",EDGE,"E19.2.0"),sQuery(id+"F9.wireOp",EDGE,"E19.2.1"),subQ11,sQuery(id+"F9.wireOp",EDGE,"E19.2.3")])],"isStart":false});var subQ14=makeQuery(id+"F4.opFillet","BLEND_EDGE",EDGE,{"blendedFrom":[makeQuery(id+"F1.opExtrude","CAP_EDGE",EDGE,{"disambiguationData":[OSD([subQ0])],"isStart":false}),subQ10],"blendedInto":[subQ10]});var subQ15=sQuery(id+"F0.wireOp",EDGE,"E2.0");Q4=makeQuery(id+"F12.opFillet","MERGE",EDGE,{"derivedFrom":[makeQuery(id+"F10.boolean.opBoolean","SPLIT",EDGE,{"disambiguationData":[topologyDisambiguationEdgeConnected([subQ1,subQ12])],"derivedFrom":subQ14}),makeQuery(id+"F10.boolean.opBoolean","SPLIT",EDGE,{"disambiguationData":[topologyDisambiguationEdgeConnected([subQ10,subQ1]),TD([makeQuery(id+"F2.opFillet","BLEND_FACE",FACE,{"disambiguationData":[OSD([subQ15,subQ7,subQ6,subQ0])]})])],"derivedFrom":subQ14}),makeQuery(id+"F10.boolean.opBoolean","SPLIT",EDGE,{"disambiguationData":[topologyDisambiguationEdgeConnected([subQ10,subQ1]),TD([makeQuery(id+"F2.opFillet","BLEND_FACE",FACE,{"disambiguationData":[OSD([subQ8,subQ7,subQ0,subQ5])]})])],"derivedFrom":subQ14})]});}
            var Q5;
            {var subQ0=sQuery(id+"F0.wireOp",EDGE,"E4.1.0");var subQ1=makeQuery(id+"F4.opFillet","BLEND_FACE",FACE,{"disambiguationData":[OSD([subQ0])]});var subQ5=sQuery(id+"F0.wireOp",EDGE,"E4.2.0");var subQ6=sQuery(id+"F0.wireOp",EDGE,"E3");var subQ7=sQuery(id+"F0.wireOp",EDGE,"E2.2");var subQ8=sQuery(id+"F0.wireOp",EDGE,"E2.1");var subQ10=makeQuery(id+"F1.opExtrude","SWEPT_FACE",FACE,{"disambiguationData":[OSD([subQ0])]});var subQ11=sQuery(id+"F9.wireOp",EDGE,"E19.2.2");var subQ12=makeQuery(id+"F10.opExtrude","CAP_FACE",FACE,{"disambiguationData":[OSD([sQuery(id+"F9.wireOp",EDGE,"E19.2.0"),sQuery(id+"F9.wireOp",EDGE,"E19.2.1"),subQ11,sQuery(id+"F9.wireOp",EDGE,"E19.2.3")])],"isStart":false});var subQ14=makeQuery(id+"F4.opFillet","BLEND_EDGE",EDGE,{"blendedFrom":[makeQuery(id+"F1.opExtrude","CAP_EDGE",EDGE,{"disambiguationData":[OSD([subQ0])],"isStart":false}),subQ10],"blendedInto":[subQ10]});var subQ15=sQuery(id+"F0.wireOp",EDGE,"E2.0");Q5=makeQuery(id+"F12.opFillet","MERGE",EDGE,{"derivedFrom":[makeQuery(id+"F11.opPattern","COPY",EDGE,{"derivedFrom":makeQuery(id+"F10.boolean.opBoolean","SPLIT",EDGE,{"disambiguationData":[topologyDisambiguationEdgeConnected([subQ1,subQ12])],"derivedFrom":subQ14}),"instanceName":"1"}),makeQuery(id+"F11.opPattern","COPY",EDGE,{"derivedFrom":makeQuery(id+"F10.boolean.opBoolean","SPLIT",EDGE,{"disambiguationData":[topologyDisambiguationEdgeConnected([subQ10,subQ1]),TD([makeQuery(id+"F2.opFillet","BLEND_FACE",FACE,{"disambiguationData":[OSD([subQ15,subQ7,subQ6,subQ0])]})])],"derivedFrom":subQ14}),"instanceName":"1"}),makeQuery(id+"F11.opPattern","COPY",EDGE,{"derivedFrom":makeQuery(id+"F10.boolean.opBoolean","SPLIT",EDGE,{"disambiguationData":[topologyDisambiguationEdgeConnected([subQ10,subQ1]),TD([makeQuery(id+"F2.opFillet","BLEND_FACE",FACE,{"disambiguationData":[OSD([subQ8,subQ7,subQ0,subQ5])]})])],"derivedFrom":subQ14}),"instanceName":"1"})]});}
            fillet(context, id + "F14", {"entities" : qUnion([Q0, Q1, Q2, Q3, Q4, Q5]), "radius" : 0.25 * mm, "tangentPropagation" : true, "allowEdgeOverflow" : false});
        }
        {
            var Q0;
            {var subQ0=sQuery(id+"F0.wireOp",EDGE,"E7.2.0");var subQ1=sQuery(id+"F0.wireOp",EDGE,"E7.1.0");var subQ2=sQuery(id+"F0.wireOp",EDGE,"E6");var subQ3=sQuery(id+"F0.wireOp",EDGE,"E4.2.0");var subQ4=sQuery(id+"F0.wireOp",EDGE,"E4.1.0");var subQ5=sQuery(id+"F0.wireOp",EDGE,"E3");var subQ8=sQuery(id+"F0.wireOp",EDGE,"E0");Q0=makeQuery(id+"F6.boolean.opBoolean","SPLIT",FACE,{"disambiguationData":[TD([makeQuery(id+"F3.opChamfer","BLEND_FACE",FACE,{"disambiguationData":[OSD([subQ2])]})])],"derivedFrom":makeQuery(id+"F1.opExtrude","CAP_FACE",FACE,{"disambiguationData":[OSD([subQ8,subQ5,subQ4,subQ3,subQ2,subQ1,subQ0])],"isStart":false})});}
            cPlane(context, id + "F15", {"entities" : qUnion([Q0]), "cplaneType" : CPlaneType.OFFSET, "offset" : 0.5 * mm, "width" : 152.4 * mm, "height" : 152.4 * mm});
        }
        {
            var Q0;
            Q0=qCreatedBy(id+"F15.planeOp",FACE);
            var sketch = newSketch(context, id + "F16", { "sketchPlane" : qUnion([Q0])});
            skCircle(sketch, "E20", {"center": v(0, 0) * mm, "radius": 11.18 * mm});
            skSolve(sketch);
        }
        {
            var Q0;
            Q0=makeQuery(id+"F16.imprint","IMPRINT",FACE,{"disambiguationData":[TD([[makeQuery(id+"F16.imprint","IMPRINT",EDGE,{"derivedFrom":sQuery(id+"F16.wireOp",EDGE,"E20")}),1.0]])]});
            extrude(context, id + "F17", {"entities" : qUnion([Q0]), "depth" : 2.54 * mm, "offsetDistance" : 25.4 * mm});
        }
        {
            var Q0;
            Q0=makeQuery(id+"F17.opExtrude","CAP_EDGE",EDGE,{"disambiguationData":[OSD([sQuery(id+"F16.wireOp",EDGE,"E20")])],"isStart":false});
            chamfer(context, id + "F18", {"entities" : qUnion([Q0]), "width" : 2.03 * mm, "tangentPropagation" : true});
        }
        {
            var Q0;
            Q0=makeQuery(id+"F17.opExtrude","CAP_FACE",FACE,{"disambiguationData":[OSD([sQuery(id+"F16.wireOp",EDGE,"E20")])],"isStart":false});
            var sketch = newSketch(context, id + "F19", { "sketchPlane" : qUnion([Q0])});
            skCircle(sketch, "E21", {"center": v(0, 4.24) * mm, "radius": 4.9 * mm});
            skCircle(sketch, "E22", {"center": v(0, 4.24) * mm, "radius": 4.27 * mm});
            skSolve(sketch);
        }
        {
            var Q0;
            Q0=makeQuery(id+"F19.imprint","IMPRINT",FACE,{"disambiguationData":[TD([[makeQuery(id+"F19.imprint","IMPRINT",EDGE,{"derivedFrom":sQuery(id+"F19.wireOp",EDGE,"E21")}),1.0]])]});
            extrude(context, id + "F20", {"entities" : qUnion([Q0]), "operationType" : NewBodyOperationType.REMOVE, "oppositeDirection" : true, "depth" : 0.76 * mm, "offsetDistance" : 25.4 * mm});
        }
        {
            var Q0;
            Q0=makeQuery(id+"F20.boolean.opBoolean","COPY",EDGE,{"derivedFrom":makeQuery(id+"F20.opExtrude","CAP_EDGE",EDGE,{"disambiguationData":[OSD([sQuery(id+"F19.wireOp",EDGE,"E21")])],"isStart":false})});
            var Q1;
            Q1=makeQuery(id+"F20.boolean.opBoolean","COPY",EDGE,{"derivedFrom":makeQuery(id+"F20.opExtrude","CAP_EDGE",EDGE,{"disambiguationData":[OSD([sQuery(id+"F19.wireOp",EDGE,"E22")])],"isStart":false})});
            chamfer(context, id + "F21", {"entities" : qUnion([Q0, Q1]), "width" : 0.25 * mm, "tangentPropagation" : true});
        }
        {
            var Q0;
            Q0=makeQuery(id+"F17.opExtrude","CAP_FACE",FACE,{"disambiguationData":[OSD([sQuery(id+"F16.wireOp",EDGE,"E20")])],"isStart":true});
            var sketch = newSketch(context, id + "F22", { "sketchPlane" : qUnion([Q0])});
            skCircle(sketch, "E23", {"center": v(0, 0) * mm, "radius": 5.46 * mm});
            skSolve(sketch);
        }
        {
            var Q0;
            Q0=makeQuery(id+"F22.imprint","IMPRINT",FACE,{"disambiguationData":[TD([[makeQuery(id+"F22.imprint","IMPRINT",EDGE,{"derivedFrom":sQuery(id+"F22.wireOp",EDGE,"E23")}),1.0]])]});
            extrude(context, id + "F23", {"entities" : qUnion([Q0]), "operationType" : NewBodyOperationType.ADD, "depth" : 0.5 * mm, "offsetDistance" : 25.4 * mm});
        }
        {
            var Q0;
            Q0=makeQuery(id+"F23.opExtrude","CAP_FACE",FACE,{"disambiguationData":[OSD([sQuery(id+"F22.wireOp",EDGE,"E23")])],"isStart":false});
            var sketch = newSketch(context, id + "F24", { "sketchPlane" : qUnion([Q0])});
            skCircle(sketch, "E24", {"center": v(0, 0) * mm, "radius": 3.94 * mm});
            skSolve(sketch);
        }
        {
            var Q0;
            Q0=makeQuery(id+"F24.imprint","IMPRINT",FACE,{"disambiguationData":[TD([[makeQuery(id+"F24.imprint","IMPRINT",EDGE,{"derivedFrom":sQuery(id+"F24.wireOp",EDGE,"E24")}),1.0]])]});
            extrude(context, id + "F25", {"entities" : qUnion([Q0]), "operationType" : NewBodyOperationType.ADD, "depth" : 2.92 * mm, "offsetDistance" : 25.4 * mm});
        }
        {
            var Q0;
            Q0=makeQuery(id+"F25.opExtrude","CAP_FACE",FACE,{"disambiguationData":[OSD([sQuery(id+"F24.wireOp",EDGE,"E24")])],"isStart":false});
            chamfer(context, id + "F26", {"entities" : qUnion([Q0]), "width" : 0.76 * mm, "tangentPropagation" : true});
        }
        {
            var Q0;
            Q0=makeQuery(id+"F25.opExtrude","CAP_FACE",FACE,{"disambiguationData":[OSD([sQuery(id+"F24.wireOp",EDGE,"E24")])],"isStart":false});
            var sketch = newSketch(context, id + "F27", { "sketchPlane" : qUnion([Q0])});
            skCircle(sketch, "E25", {"center": v(0, 0) * mm, "radius": 2.46 * mm});
            skSolve(sketch);
        }
        {
            var Q0;
            Q0=makeQuery(id+"F27.imprint","IMPRINT",FACE,{"disambiguationData":[TD([[makeQuery(id+"F27.imprint","IMPRINT",EDGE,{"derivedFrom":sQuery(id+"F27.wireOp",EDGE,"E25")}),1.0]])]});
            extrude(context, id + "F28", {"entities" : qUnion([Q0]), "operationType" : NewBodyOperationType.REMOVE, "oppositeDirection" : true, "depth" : 2.92 * mm, "offsetDistance" : 25.4 * mm});
        }
        {
            var Q0;
            Q0=makeQuery(id+"F28.boolean.opBoolean","COPY",EDGE,{"derivedFrom":makeQuery(id+"F28.opExtrude","CAP_EDGE",EDGE,{"disambiguationData":[OSD([sQuery(id+"F27.wireOp",EDGE,"E25")])],"isStart":false})});
            fillet(context, id + "F29", {"entities" : qUnion([Q0]), "radius" : 1.52 * mm, "tangentPropagation" : true, "allowEdgeOverflow" : false});
        }
    });
